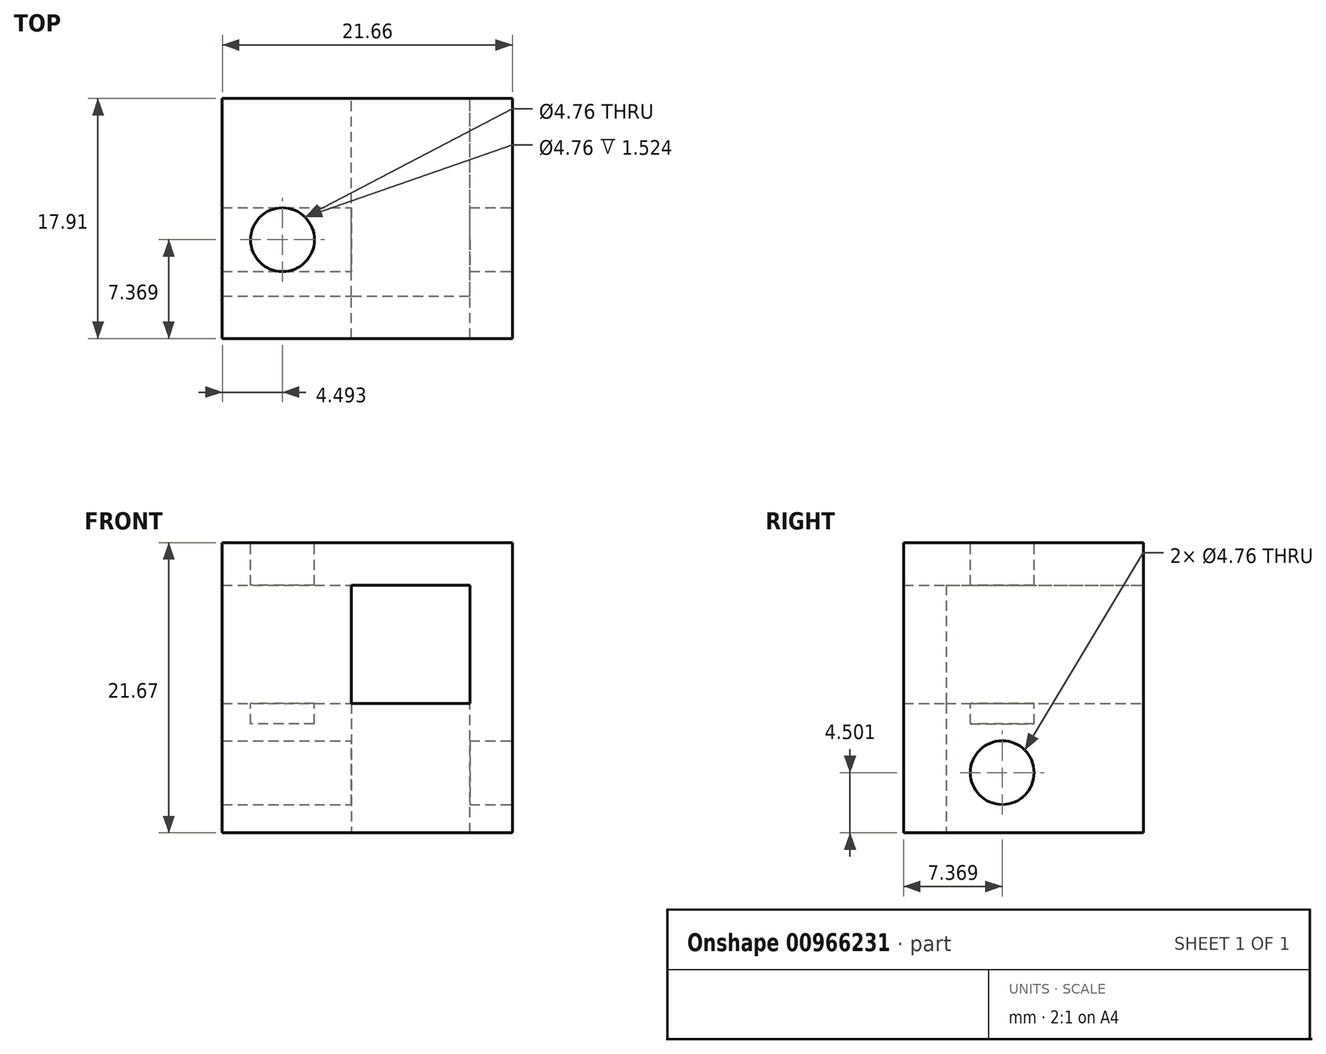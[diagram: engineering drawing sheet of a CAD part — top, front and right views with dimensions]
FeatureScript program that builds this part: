
annotation { "Feature Type Name" : "Feature", "Feature Type Description" : "" }
export const myFeature = defineFeature(function(context is Context, id is Id, definition is map)
    precondition{}
    {
        {
            var Q0;
            Q0=qCreatedBy(makeId("Front.planeOp"),FACE);
            var sketch = newSketch(context, id + "F0", { "sketchPlane" : qUnion([Q0])});
            skLineSegment(sketch, "E0.bottom", {"start": v(-32.27, -22.25) * mm, "end": v(-10.6, -22.25) * mm});
            skLineSegment(sketch, "E0.top", {"start": v(-32.27, -43.92) * mm, "end": v(-10.6, -43.92) * mm});
            skLineSegment(sketch, "E0.left", {"start": v(-32.27, -22.25) * mm, "end": v(-32.27, -43.92) * mm});
            skLineSegment(sketch, "E0.right", {"start": v(-10.6, -22.25) * mm, "end": v(-10.6, -43.92) * mm});
            skSolve(sketch);
        }
        {
            var Q0;
            Q0=makeQuery(id+"F0.imprint","IMPRINT",FACE,{"disambiguationData":[TD([[makeQuery(id+"F0.imprint","IMPRINT",EDGE,{"derivedFrom":sQuery(id+"F0.wireOp",EDGE,"E0.bottom")}),-1.0]])]});
            extrude(context, id + "F1", {"entities" : qUnion([Q0]), "depth" : 1 / 203.2 * mm});
        }
        {
            var Q0;
            Q0=makeQuery(id+"F1.opExtrude","CAP_FACE",FACE,{"disambiguationData":[OSD([sQuery(id+"F0.wireOp",EDGE,"E0.bottom"),sQuery(id+"F0.wireOp",EDGE,"E0.top"),sQuery(id+"F0.wireOp",EDGE,"E0.left"),sQuery(id+"F0.wireOp",EDGE,"E0.right")])],"isStart":false});
            var sketch = newSketch(context, id + "F2", { "sketchPlane" : qUnion([Q0])});
            skLineSegment(sketch, "E1.bottom", {"start": v(-32.27, -34.26) * mm, "end": v(-22.62, -34.26) * mm});
            skLineSegment(sketch, "E1.top", {"start": v(-32.27, -43.92) * mm, "end": v(-22.62, -43.92) * mm});
            skLineSegment(sketch, "E1.left", {"start": v(-32.27, -34.26) * mm, "end": v(-32.27, -43.92) * mm});
            skLineSegment(sketch, "E1.right", {"start": v(-22.62, -34.26) * mm, "end": v(-22.62, -43.92) * mm});
            skLineSegment(sketch, "E2", {"start": v(-22.62, -43.92) * mm, "end": v(-13.78, -43.92) * mm});
            skLineSegment(sketch, "E3", {"start": v(-32.27, -34.26) * mm, "end": v(-32.27, -25.42) * mm});
            skLineSegment(sketch, "E4.bottom", {"start": v(-32.27, -25.42) * mm, "end": v(-13.78, -25.42) * mm});
            skLineSegment(sketch, "E4.top", {"start": v(-32.27, -22.25) * mm, "end": v(-13.78, -22.25) * mm});
            skLineSegment(sketch, "E4.left", {"start": v(-32.27, -25.42) * mm, "end": v(-32.27, -22.25) * mm});
            skLineSegment(sketch, "E4.right", {"start": v(-13.78, -25.42) * mm, "end": v(-13.78, -22.25) * mm});
            skLineSegment(sketch, "E5.bottom", {"start": v(-13.78, -43.92) * mm, "end": v(-10.6, -43.92) * mm});
            skLineSegment(sketch, "E5.top", {"start": v(-13.78, -22.25) * mm, "end": v(-10.6, -22.25) * mm});
            skLineSegment(sketch, "E5.left", {"start": v(-13.78, -43.92) * mm, "end": v(-13.78, -22.25) * mm});
            skLineSegment(sketch, "E5.right", {"start": v(-10.6, -43.92) * mm, "end": v(-10.6, -22.25) * mm});
            skSolve(sketch);
        }
        {
            var Q0;
            {var subQ0=sQuery(id+"F2.wireOp",EDGE,"E4.bottom");Q0=makeQuery(id+"F2.imprint","IMPRINT",FACE,{"disambiguationData":[TD([[makeQuery(id+"F2.imprint","IMPRINT",EDGE,{"derivedFrom":subQ0}),1.0]])]});}
            var Q1;
            {var subQ3=sQuery(id+"F2.wireOp",EDGE,"E5.bottom");Q1=makeQuery(id+"F2.imprint","IMPRINT",FACE,{"disambiguationData":[TD([[makeQuery(id+"F2.imprint","IMPRINT",EDGE,{"derivedFrom":subQ3}),1.0]])]});}
            var Q2;
            Q2=makeQuery(id+"F2.imprint","IMPRINT",FACE,{"disambiguationData":[TD([[makeQuery(id+"F2.imprint","IMPRINT",EDGE,{"derivedFrom":sQuery(id+"F2.wireOp",EDGE,"E1.bottom")}),-1.0]])]});
            extrude(context, id + "F3", {"entities" : qUnion([Q0, Q1, Q2]), "operationType" : NewBodyOperationType.ADD, "depth" : 14.73 * mm});
        }
        {
            var Q0;
            Q0=makeQuery(id+"F3.boolean.opBoolean","MERGE",FACE,{"derivedFrom":[makeQuery(id+"F1.opExtrude","SWEPT_FACE",FACE,{"disambiguationData":[OSD([sQuery(id+"F0.wireOp",EDGE,"E0.bottom")])]}),makeQuery(id+"F3.opExtrude","SWEPT_FACE",FACE,{"disambiguationData":[OSD([sQuery(id+"F2.wireOp",EDGE,"E4.top"),sQuery(id+"F2.wireOp",EDGE,"E5.top")])]})]});
            var sketch = newSketch(context, id + "F4", { "sketchPlane" : qUnion([Q0])});
            skLineSegment(sketch, "E6", {"start": v(-32.27, -17.9) * mm, "end": v(-32.27, -10.54) * mm});
            skLineSegment(sketch, "E7", {"start": v(-32.27, -10.54) * mm, "end": v(-27.78, -10.54) * mm});
            skCircle(sketch, "E8", {"center": v(-27.78, -10.54) * mm, "radius": 2.38 * mm});
            skSolve(sketch);
        }
        {
            var Q0;
            Q0=makeQuery(id+"F4.imprint","IMPRINT",FACE,{"disambiguationData":[TD([[makeQuery(id+"F4.imprint","IMPRINT",EDGE,{"derivedFrom":sQuery(id+"F4.wireOp",EDGE,"E8")}),1.0]])]});
            extrude(context, id + "F5", {"entities" : qUnion([Q0]), "operationType" : NewBodyOperationType.REMOVE, "oppositeDirection" : true, "depth" : 13.54 * mm});
        }
        {
            var Q0;
            Q0=makeQuery(id+"F3.boolean.opBoolean","MERGE",FACE,{"derivedFrom":[makeQuery(id+"F1.opExtrude","SWEPT_FACE",FACE,{"disambiguationData":[OSD([sQuery(id+"F0.wireOp",EDGE,"E0.right")])]}),makeQuery(id+"F3.opExtrude","SWEPT_FACE",FACE,{"disambiguationData":[OSD([sQuery(id+"F2.wireOp",EDGE,"E5.right")])]})]});
            var sketch = newSketch(context, id + "F6", { "sketchPlane" : qUnion([Q0])});
            skLineSegment(sketch, "E9", {"start": v(-17.9, -43.92) * mm, "end": v(-10.54, -43.92) * mm});
            skLineSegment(sketch, "E10", {"start": v(-10.54, -39.42) * mm, "end": v(-10.54, -43.92) * mm});
            skCircle(sketch, "E11", {"center": v(-10.54, -39.42) * mm, "radius": 2.38 * mm});
            skSolve(sketch);
        }
        {
            var Q0;
            Q0=makeQuery(id+"F6.imprint","IMPRINT",FACE,{"disambiguationData":[TD([[makeQuery(id+"F6.imprint","IMPRINT",EDGE,{"derivedFrom":sQuery(id+"F6.wireOp",EDGE,"E11")}),1.0]])]});
            extrude(context, id + "F7", {"entities" : qUnion([Q0]), "operationType" : NewBodyOperationType.REMOVE, "oppositeDirection" : true, "depth" : 25.4 * mm});
        }
        {
            var Q0;
            Q0=makeQuery(id+"F3.opExtrude","CAP_FACE",FACE,{"disambiguationData":[OSD([sQuery(id+"F2.wireOp",EDGE,"E4.bottom"),sQuery(id+"F2.wireOp",EDGE,"E4.top"),sQuery(id+"F2.wireOp",EDGE,"E4.left"),sQuery(id+"F2.wireOp",EDGE,"E5.bottom"),sQuery(id+"F2.wireOp",EDGE,"E5.top"),sQuery(id+"F2.wireOp",EDGE,"E5.left"),sQuery(id+"F2.wireOp",EDGE,"E5.right")])],"isStart":false});
            var sketch = newSketch(context, id + "F8", { "sketchPlane" : qUnion([Q0])});
            skLineSegment(sketch, "E12.bottom", {"start": v(-10.6, -22.25) * mm, "end": v(-32.27, -22.25) * mm});
            skLineSegment(sketch, "E12.top", {"start": v(-10.6, -43.92) * mm, "end": v(-32.27, -43.92) * mm});
            skLineSegment(sketch, "E12.left", {"start": v(-10.6, -22.25) * mm, "end": v(-10.6, -43.92) * mm});
            skLineSegment(sketch, "E12.right", {"start": v(-32.27, -22.25) * mm, "end": v(-32.27, -43.92) * mm});
            skLineSegment(sketch, "E13.bottom", {"start": v(-13.78, -25.42) * mm, "end": v(-22.62, -25.42) * mm});
            skLineSegment(sketch, "E13.top", {"start": v(-13.78, -34.26) * mm, "end": v(-22.62, -34.26) * mm});
            skLineSegment(sketch, "E13.left", {"start": v(-13.78, -25.42) * mm, "end": v(-13.78, -34.26) * mm});
            skLineSegment(sketch, "E13.right", {"start": v(-22.62, -25.42) * mm, "end": v(-22.62, -34.26) * mm});
            skSolve(sketch);
        }
        {
            var Q0;
            {var subQ0=sQuery(id+"F8.wireOp",EDGE,"E13.bottom");Q0=makeQuery(id+"F8.imprint","IMPRINT",FACE,{"disambiguationData":[TD([[makeQuery(id+"F8.imprint","IMPRINT",EDGE,{"derivedFrom":subQ0}),1.0]])]});}
            var Q1;
            {var subQ3=sQuery(id+"F8.wireOp",EDGE,"E12.top");Q1=makeQuery(id+"F8.imprint","IMPRINT",FACE,{"disambiguationData":[TD([[makeQuery(id+"F8.imprint","IMPRINT",EDGE,{"derivedFrom":subQ3}),-1.0]])]});}
            extrude(context, id + "F9", {"entities" : qUnion([Q0, Q1]), "operationType" : NewBodyOperationType.ADD, "depth" : 3.17 * mm});
        }
    });
